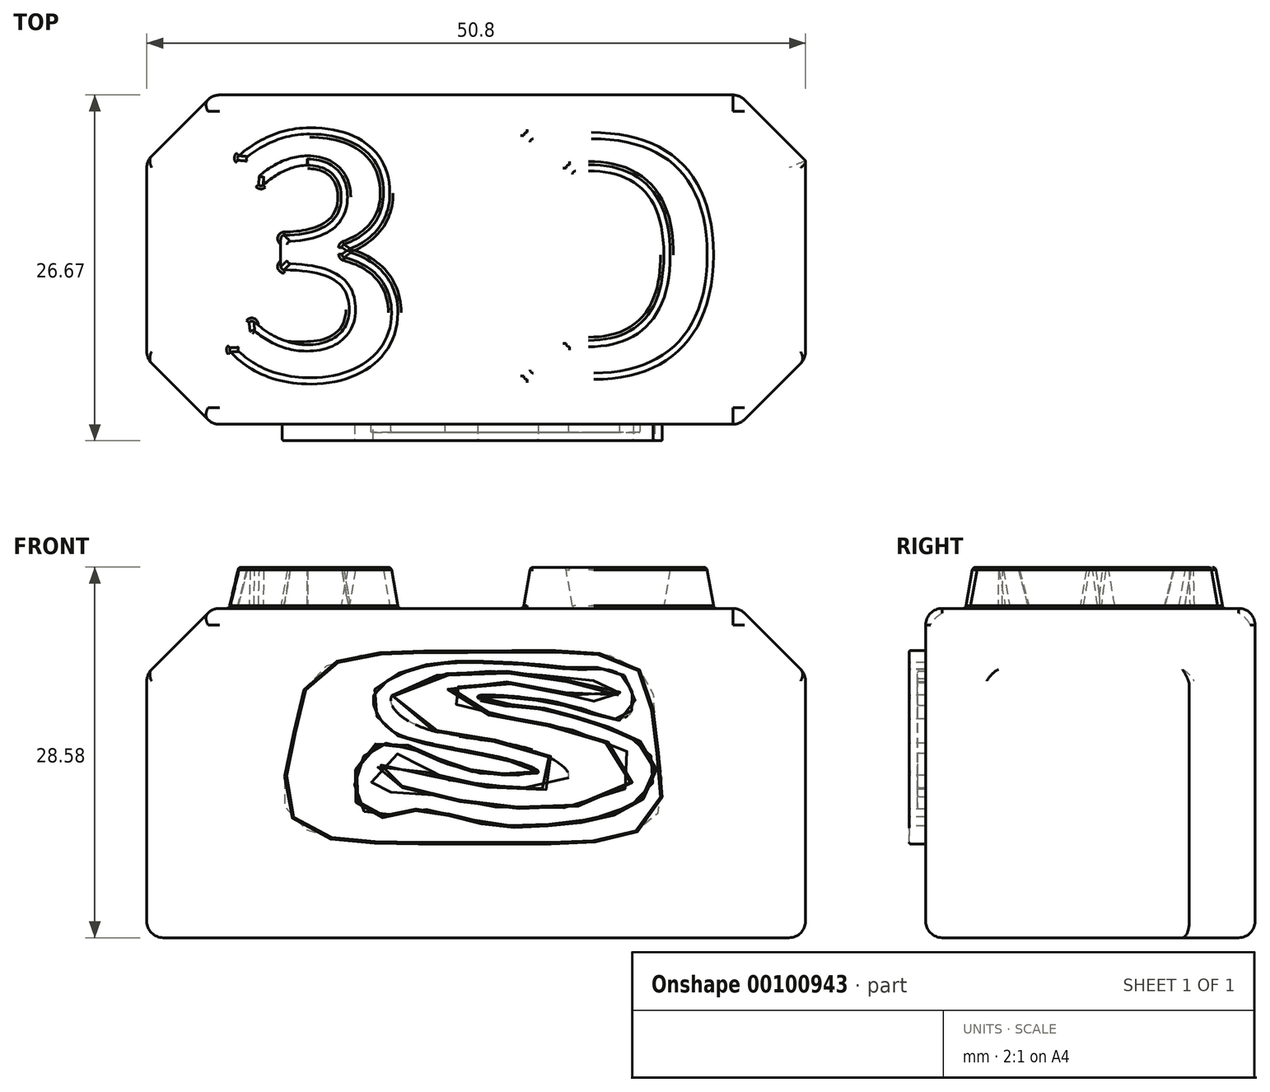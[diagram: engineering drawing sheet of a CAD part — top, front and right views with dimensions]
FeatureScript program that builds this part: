
annotation { "Feature Type Name" : "Feature", "Feature Type Description" : "" }
export const myFeature = defineFeature(function(context is Context, id is Id, definition is map)
    precondition{}
    {
        {
            var Q0;
            Q0=qCreatedBy(makeId("Top.planeOp"),FACE);
            var sketch = newSketch(context, id + "F0", { "sketchPlane" : qUnion([Q0])});
            skLineSegment(sketch, "E0.bottom", {"start": v(0, 0) * mm, "end": v(50.8, 0) * mm});
            skLineSegment(sketch, "E0.top", {"start": v(0, -25.4) * mm, "end": v(50.8, -25.4) * mm});
            skLineSegment(sketch, "E0.left", {"start": v(0, 0) * mm, "end": v(0, -25.4) * mm});
            skLineSegment(sketch, "E0.right", {"start": v(50.8, 0) * mm, "end": v(50.8, -25.4) * mm});
            skSolve(sketch);
        }
        {
            var Q0;
            Q0=makeQuery(id+"F0.imprint","IMPRINT",FACE,{"disambiguationData":[TD([[makeQuery(id+"F0.imprint","IMPRINT",EDGE,{"derivedFrom":sQuery(id+"F0.wireOp",EDGE,"E0.bottom")}),-1.0]])]});
            extrude(context, id + "F1", {"entities" : qUnion([Q0]), "depth" : 25.4 * mm});
        }
        {
            var Q0;
            Q0=makeQuery(id+"F1.opExtrude","CAP_EDGE",EDGE,{"disambiguationData":[OSD([sQuery(id+"F0.wireOp",EDGE,"E0.left")])],"isStart":false});
            var Q1;
            Q1=makeQuery(id+"F1.opExtrude","CAP_EDGE",EDGE,{"disambiguationData":[OSD([sQuery(id+"F0.wireOp",EDGE,"E0.right")])],"isStart":false});
            var Q2;
            Q2=makeQuery(id+"F1.opExtrude","SWEPT_EDGE",EDGE,{"disambiguationData":[OSD([sQuery(id+"F0.wireOp",EDGE,"E0.top"),sQuery(id+"F0.wireOp",EDGE,"E0.left")])]});
            var Q3;
            Q3=makeQuery(id+"F1.opExtrude","SWEPT_EDGE",EDGE,{"disambiguationData":[OSD([sQuery(id+"F0.wireOp",EDGE,"E0.top"),sQuery(id+"F0.wireOp",EDGE,"E0.right")])]});
            var Q4;
            Q4=makeQuery(id+"F1.opExtrude","SWEPT_EDGE",EDGE,{"disambiguationData":[OSD([sQuery(id+"F0.wireOp",EDGE,"E0.bottom"),sQuery(id+"F0.wireOp",EDGE,"E0.right")])]});
            var Q5;
            Q5=makeQuery(id+"F1.opExtrude","SWEPT_EDGE",EDGE,{"disambiguationData":[OSD([sQuery(id+"F0.wireOp",EDGE,"E0.bottom"),sQuery(id+"F0.wireOp",EDGE,"E0.left")])]});
            chamfer(context, id + "F2", {"entities" : qUnion([Q0, Q1, Q2, Q3, Q4, Q5]), "width" : 5.08 * mm, "tangentPropagation" : true});
        }
        {
            var Q0;
            Q0=makeQuery(id+"F1.opExtrude","CAP_EDGE",EDGE,{"disambiguationData":[OSD([sQuery(id+"F0.wireOp",EDGE,"E0.top")])],"isStart":false});
            var Q1;
            Q1=makeQuery(id+"F1.opExtrude","CAP_EDGE",EDGE,{"disambiguationData":[OSD([sQuery(id+"F0.wireOp",EDGE,"E0.bottom")])],"isStart":false});
            var Q2;
            {var subQ0=sQuery(id+"F0.wireOp",EDGE,"E0.right");var subQ1=sQuery(id+"F0.wireOp",EDGE,"E0.left");var subQ2=sQuery(id+"F0.wireOp",EDGE,"E0.top");var subQ3=sQuery(id+"F0.wireOp",EDGE,"E0.bottom");Q2=makeQuery(id+"F2.opChamfer","BLEND_EDGE",EDGE,{"blendedFrom":[makeQuery(id+"F1.opExtrude","CAP_EDGE",EDGE,{"disambiguationData":[OSD([subQ0])],"isStart":false}),makeQuery(id+"FMAaeaN72eKezCo_1.boolean.opBoolean","SPLIT",FACE,{"disambiguationData":[TD([makeQuery(id+"F1.opExtrude","SWEPT_FACE",FACE,{"disambiguationData":[OSD([subQ3])]})])],"derivedFrom":makeQuery(id+"F1.opExtrude","CAP_FACE",FACE,{"disambiguationData":[OSD([subQ3,subQ2,subQ1,subQ0])],"isStart":false})})],"blendedInto":[makeQuery(id+"FMAaeaN72eKezCo_1.boolean.opBoolean","SPLIT",FACE,{"disambiguationData":[TD([makeQuery(id+"F1.opExtrude","SWEPT_FACE",FACE,{"disambiguationData":[OSD([subQ3])]})])],"derivedFrom":makeQuery(id+"F1.opExtrude","CAP_FACE",FACE,{"disambiguationData":[OSD([subQ3,subQ2,subQ1,subQ0])],"isStart":false})})]});}
            var Q3;
            {var subQ0=sQuery(id+"F0.wireOp",EDGE,"E0.right");Q3=makeQuery(id+"F2.opChamfer","BLEND_EDGE",EDGE,{"blendedFrom":[makeQuery(id+"F1.opExtrude","SWEPT_EDGE",EDGE,{"disambiguationData":[OSD([sQuery(id+"F0.wireOp",EDGE,"E0.bottom"),subQ0])]}),makeQuery(id+"F1.opExtrude","CAP_EDGE",EDGE,{"disambiguationData":[OSD([subQ0])],"isStart":false})],"blendedInto":[]});}
            var Q4;
            {var subQ0=sQuery(id+"F0.wireOp",EDGE,"E0.right");Q4=makeQuery(id+"F2.opChamfer","BLEND_EDGE",EDGE,{"blendedFrom":[makeQuery(id+"F1.opExtrude","SWEPT_EDGE",EDGE,{"disambiguationData":[OSD([sQuery(id+"F0.wireOp",EDGE,"E0.top"),subQ0])]}),makeQuery(id+"F1.opExtrude","CAP_EDGE",EDGE,{"disambiguationData":[OSD([subQ0])],"isStart":false})],"blendedInto":[]});}
            var Q5;
            {var subQ0=sQuery(id+"F0.wireOp",EDGE,"E0.top");Q5=makeQuery(id+"F2.opChamfer","BLEND_EDGE",EDGE,{"blendedFrom":[makeQuery(id+"F1.opExtrude","SWEPT_EDGE",EDGE,{"disambiguationData":[OSD([subQ0,sQuery(id+"F0.wireOp",EDGE,"E0.right")])]}),makeQuery(id+"F1.opExtrude","SWEPT_FACE",FACE,{"disambiguationData":[OSD([subQ0])]})],"blendedInto":[makeQuery(id+"F1.opExtrude","SWEPT_FACE",FACE,{"disambiguationData":[OSD([subQ0])]})]});}
            var Q6;
            Q6=makeQuery(id+"F1.opExtrude","CAP_EDGE",EDGE,{"disambiguationData":[OSD([sQuery(id+"F0.wireOp",EDGE,"E0.right")])],"isStart":true});
            var Q7;
            {var subQ0=sQuery(id+"F0.wireOp",EDGE,"E0.top");Q7=makeQuery(id+"F2.opChamfer","BLEND_EDGE",EDGE,{"blendedFrom":[makeQuery(id+"F1.opExtrude","SWEPT_EDGE",EDGE,{"disambiguationData":[OSD([subQ0,sQuery(id+"F0.wireOp",EDGE,"E0.left")])]}),makeQuery(id+"F1.opExtrude","SWEPT_FACE",FACE,{"disambiguationData":[OSD([subQ0])]})],"blendedInto":[makeQuery(id+"F1.opExtrude","SWEPT_FACE",FACE,{"disambiguationData":[OSD([subQ0])]})]});}
            var Q8;
            {var subQ0=sQuery(id+"F0.wireOp",EDGE,"E0.left");Q8=makeQuery(id+"F2.opChamfer","BLEND_EDGE",EDGE,{"blendedFrom":[makeQuery(id+"F1.opExtrude","SWEPT_EDGE",EDGE,{"disambiguationData":[OSD([sQuery(id+"F0.wireOp",EDGE,"E0.top"),subQ0])]}),makeQuery(id+"F1.opExtrude","SWEPT_FACE",FACE,{"disambiguationData":[OSD([subQ0])]})],"blendedInto":[makeQuery(id+"F1.opExtrude","SWEPT_FACE",FACE,{"disambiguationData":[OSD([subQ0])]})]});}
            var Q9;
            {var subQ0=sQuery(id+"F0.wireOp",EDGE,"E0.left");Q9=makeQuery(id+"F2.opChamfer","BLEND_EDGE",EDGE,{"blendedFrom":[makeQuery(id+"F1.opExtrude","SWEPT_EDGE",EDGE,{"disambiguationData":[OSD([sQuery(id+"F0.wireOp",EDGE,"E0.top"),subQ0])]}),makeQuery(id+"F1.opExtrude","CAP_EDGE",EDGE,{"disambiguationData":[OSD([subQ0])],"isStart":false})],"blendedInto":[]});}
            var Q10;
            {var subQ0=sQuery(id+"F0.wireOp",EDGE,"E0.right");var subQ1=sQuery(id+"F0.wireOp",EDGE,"E0.left");var subQ2=sQuery(id+"F0.wireOp",EDGE,"E0.top");var subQ3=sQuery(id+"F0.wireOp",EDGE,"E0.bottom");Q10=makeQuery(id+"F2.opChamfer","BLEND_EDGE",EDGE,{"blendedFrom":[makeQuery(id+"F1.opExtrude","CAP_EDGE",EDGE,{"disambiguationData":[OSD([subQ1])],"isStart":false}),makeQuery(id+"FMAaeaN72eKezCo_1.boolean.opBoolean","SPLIT",FACE,{"disambiguationData":[TD([makeQuery(id+"F1.opExtrude","SWEPT_FACE",FACE,{"disambiguationData":[OSD([subQ3])]})])],"derivedFrom":makeQuery(id+"F1.opExtrude","CAP_FACE",FACE,{"disambiguationData":[OSD([subQ3,subQ2,subQ1,subQ0])],"isStart":false})})],"blendedInto":[makeQuery(id+"FMAaeaN72eKezCo_1.boolean.opBoolean","SPLIT",FACE,{"disambiguationData":[TD([makeQuery(id+"F1.opExtrude","SWEPT_FACE",FACE,{"disambiguationData":[OSD([subQ3])]})])],"derivedFrom":makeQuery(id+"F1.opExtrude","CAP_FACE",FACE,{"disambiguationData":[OSD([subQ3,subQ2,subQ1,subQ0])],"isStart":false})})]});}
            var Q11;
            {var subQ0=sQuery(id+"F0.wireOp",EDGE,"E0.left");Q11=makeQuery(id+"F2.opChamfer","BLEND_EDGE",EDGE,{"blendedFrom":[makeQuery(id+"F1.opExtrude","CAP_EDGE",EDGE,{"disambiguationData":[OSD([subQ0])],"isStart":false}),makeQuery(id+"F1.opExtrude","SWEPT_FACE",FACE,{"disambiguationData":[OSD([subQ0])]})],"blendedInto":[makeQuery(id+"F1.opExtrude","SWEPT_FACE",FACE,{"disambiguationData":[OSD([subQ0])]})]});}
            var Q12;
            {var subQ0=sQuery(id+"F0.wireOp",EDGE,"E0.left");Q12=makeQuery(id+"F2.opChamfer","BLEND_EDGE",EDGE,{"blendedFrom":[makeQuery(id+"F1.opExtrude","SWEPT_EDGE",EDGE,{"disambiguationData":[OSD([sQuery(id+"F0.wireOp",EDGE,"E0.bottom"),subQ0])]}),makeQuery(id+"F1.opExtrude","CAP_EDGE",EDGE,{"disambiguationData":[OSD([subQ0])],"isStart":false})],"blendedInto":[]});}
            var Q13;
            {var subQ0=sQuery(id+"F0.wireOp",EDGE,"E0.left");Q13=makeQuery(id+"F2.opChamfer","BLEND_EDGE",EDGE,{"blendedFrom":[makeQuery(id+"F1.opExtrude","SWEPT_EDGE",EDGE,{"disambiguationData":[OSD([sQuery(id+"F0.wireOp",EDGE,"E0.bottom"),subQ0])]}),makeQuery(id+"F1.opExtrude","SWEPT_FACE",FACE,{"disambiguationData":[OSD([subQ0])]})],"blendedInto":[makeQuery(id+"F1.opExtrude","SWEPT_FACE",FACE,{"disambiguationData":[OSD([subQ0])]})]});}
            var Q14;
            {var subQ0=sQuery(id+"F0.wireOp",EDGE,"E0.bottom");Q14=makeQuery(id+"F2.opChamfer","BLEND_EDGE",EDGE,{"blendedFrom":[makeQuery(id+"F1.opExtrude","SWEPT_EDGE",EDGE,{"disambiguationData":[OSD([subQ0,sQuery(id+"F0.wireOp",EDGE,"E0.left")])]}),makeQuery(id+"F1.opExtrude","SWEPT_FACE",FACE,{"disambiguationData":[OSD([subQ0])]})],"blendedInto":[makeQuery(id+"F1.opExtrude","SWEPT_FACE",FACE,{"disambiguationData":[OSD([subQ0])]})]});}
            var Q15;
            {var subQ0=sQuery(id+"F0.wireOp",EDGE,"E0.bottom");Q15=makeQuery(id+"F2.opChamfer","BLEND_EDGE",EDGE,{"blendedFrom":[makeQuery(id+"F1.opExtrude","SWEPT_EDGE",EDGE,{"disambiguationData":[OSD([subQ0,sQuery(id+"F0.wireOp",EDGE,"E0.right")])]}),makeQuery(id+"F1.opExtrude","SWEPT_FACE",FACE,{"disambiguationData":[OSD([subQ0])]})],"blendedInto":[makeQuery(id+"F1.opExtrude","SWEPT_FACE",FACE,{"disambiguationData":[OSD([subQ0])]})]});}
            var Q16;
            {var subQ0=sQuery(id+"F0.wireOp",EDGE,"E0.right");Q16=makeQuery(id+"F2.opChamfer","BLEND_EDGE",EDGE,{"blendedFrom":[makeQuery(id+"F1.opExtrude","SWEPT_EDGE",EDGE,{"disambiguationData":[OSD([sQuery(id+"F0.wireOp",EDGE,"E0.top"),subQ0])]}),makeQuery(id+"F1.opExtrude","SWEPT_FACE",FACE,{"disambiguationData":[OSD([subQ0])]})],"blendedInto":[makeQuery(id+"F1.opExtrude","SWEPT_FACE",FACE,{"disambiguationData":[OSD([subQ0])]})]});}
            var Q17;
            {var subQ0=sQuery(id+"F0.wireOp",EDGE,"E0.right");Q17=makeQuery(id+"F2.opChamfer","BLEND_EDGE",EDGE,{"blendedFrom":[makeQuery(id+"F1.opExtrude","CAP_EDGE",EDGE,{"disambiguationData":[OSD([subQ0])],"isStart":false}),makeQuery(id+"F1.opExtrude","SWEPT_FACE",FACE,{"disambiguationData":[OSD([subQ0])]})],"blendedInto":[makeQuery(id+"F1.opExtrude","SWEPT_FACE",FACE,{"disambiguationData":[OSD([subQ0])]})]});}
            var Q18;
            {var subQ0=sQuery(id+"F0.wireOp",EDGE,"E0.left");var subQ1=sQuery(id+"F0.wireOp",EDGE,"E0.bottom");Q18=makeQuery(id+"F2.opChamfer","BLEND_EDGE",EDGE,{"blendedFrom":[makeQuery(id+"F1.opExtrude","SWEPT_EDGE",EDGE,{"disambiguationData":[OSD([subQ1,subQ0])]}),makeQuery(id+"F1.opExtrude","CAP_FACE",FACE,{"disambiguationData":[OSD([subQ1,sQuery(id+"F0.wireOp",EDGE,"E0.top"),subQ0,sQuery(id+"F0.wireOp",EDGE,"E0.right")])],"isStart":true})],"blendedInto":[makeQuery(id+"F1.opExtrude","CAP_FACE",FACE,{"disambiguationData":[OSD([subQ1,sQuery(id+"F0.wireOp",EDGE,"E0.top"),subQ0,sQuery(id+"F0.wireOp",EDGE,"E0.right")])],"isStart":true})]});}
            var Q19;
            Q19=makeQuery(id+"F1.opExtrude","CAP_EDGE",EDGE,{"disambiguationData":[OSD([sQuery(id+"F0.wireOp",EDGE,"E0.left")])],"isStart":true});
            var Q20;
            Q20=makeQuery(id+"F1.opExtrude","CAP_EDGE",EDGE,{"disambiguationData":[OSD([sQuery(id+"F0.wireOp",EDGE,"E0.bottom")])],"isStart":true});
            var Q21;
            {var subQ0=sQuery(id+"F0.wireOp",EDGE,"E0.right");var subQ1=sQuery(id+"F0.wireOp",EDGE,"E0.bottom");Q21=makeQuery(id+"F2.opChamfer","BLEND_EDGE",EDGE,{"blendedFrom":[makeQuery(id+"F1.opExtrude","SWEPT_EDGE",EDGE,{"disambiguationData":[OSD([subQ1,subQ0])]}),makeQuery(id+"F1.opExtrude","CAP_FACE",FACE,{"disambiguationData":[OSD([subQ1,sQuery(id+"F0.wireOp",EDGE,"E0.top"),sQuery(id+"F0.wireOp",EDGE,"E0.left"),subQ0])],"isStart":true})],"blendedInto":[makeQuery(id+"F1.opExtrude","CAP_FACE",FACE,{"disambiguationData":[OSD([subQ1,sQuery(id+"F0.wireOp",EDGE,"E0.top"),sQuery(id+"F0.wireOp",EDGE,"E0.left"),subQ0])],"isStart":true})]});}
            var Q22;
            {var subQ0=sQuery(id+"F0.wireOp",EDGE,"E0.right");var subQ1=sQuery(id+"F0.wireOp",EDGE,"E0.top");Q22=makeQuery(id+"F2.opChamfer","BLEND_EDGE",EDGE,{"blendedFrom":[makeQuery(id+"F1.opExtrude","SWEPT_EDGE",EDGE,{"disambiguationData":[OSD([subQ1,subQ0])]}),makeQuery(id+"F1.opExtrude","CAP_FACE",FACE,{"disambiguationData":[OSD([sQuery(id+"F0.wireOp",EDGE,"E0.bottom"),subQ1,sQuery(id+"F0.wireOp",EDGE,"E0.left"),subQ0])],"isStart":true})],"blendedInto":[makeQuery(id+"F1.opExtrude","CAP_FACE",FACE,{"disambiguationData":[OSD([sQuery(id+"F0.wireOp",EDGE,"E0.bottom"),subQ1,sQuery(id+"F0.wireOp",EDGE,"E0.left"),subQ0])],"isStart":true})]});}
            var Q23;
            Q23=makeQuery(id+"F1.opExtrude","CAP_EDGE",EDGE,{"disambiguationData":[OSD([sQuery(id+"F0.wireOp",EDGE,"E0.top")])],"isStart":true});
            var Q24;
            {var subQ0=sQuery(id+"F0.wireOp",EDGE,"E0.left");var subQ1=sQuery(id+"F0.wireOp",EDGE,"E0.top");Q24=makeQuery(id+"F2.opChamfer","BLEND_EDGE",EDGE,{"blendedFrom":[makeQuery(id+"F1.opExtrude","SWEPT_EDGE",EDGE,{"disambiguationData":[OSD([subQ1,subQ0])]}),makeQuery(id+"F1.opExtrude","CAP_FACE",FACE,{"disambiguationData":[OSD([sQuery(id+"F0.wireOp",EDGE,"E0.bottom"),subQ1,subQ0,sQuery(id+"F0.wireOp",EDGE,"E0.right")])],"isStart":true})],"blendedInto":[makeQuery(id+"F1.opExtrude","CAP_FACE",FACE,{"disambiguationData":[OSD([sQuery(id+"F0.wireOp",EDGE,"E0.bottom"),subQ1,subQ0,sQuery(id+"F0.wireOp",EDGE,"E0.right")])],"isStart":true})]});}
            fillet(context, id + "F3", {"entities" : qUnion([Q0, Q1, Q2, Q3, Q4, Q5, Q6, Q7, Q8, Q9, Q10, Q11, Q12, Q13, Q14, Q15, Q16, Q17, Q18, Q19, Q20, Q21, Q22, Q23, Q24]), "radius" : 1.27 * mm, "tangentPropagation" : true, "allowEdgeOverflow" : false});
        }
        {
            var Q0;
            Q0=makeQuery(id+"F1.opExtrude","CAP_FACE",FACE,{"disambiguationData":[OSD([sQuery(id+"F0.wireOp",EDGE,"E0.bottom"),sQuery(id+"F0.wireOp",EDGE,"E0.top"),sQuery(id+"F0.wireOp",EDGE,"E0.left"),sQuery(id+"F0.wireOp",EDGE,"E0.right")])],"isStart":false});
            var sketch = newSketch(context, id + "F4", { "sketchPlane" : qUnion([Q0])});
            skText(sketch, "E1", { "text": "3 D", "fontName": "NotoSansCJKsc-Bold.otf"});
            const initialGuessF4  = {"E1": [0.0056, -0.02197, 1, 0, 0.0186]};
            skSetInitialGuess(sketch, initialGuessF4);
            skSolve(sketch);
        }
        {
            var Q0;
            Q0 = qSketchRegion(id + "F4", true);
            extrude(context, id + "F5", {"entities" : qUnion([Q0]), "operationType" : NewBodyOperationType.ADD, "depth" : 3.17 * mm, "hasDraft" : true, "draftAngle" : 10 * degree, "draftPullDirection" : true});
        }
        {
            var Q0;
            Q0=makeQuery(id+"F5.opExtrude","CAP_FACE",FACE,{"disambiguationData":[OSD([sQuery(id+"F4.wireOp",EDGE,"E1.sketch_text.stroke-0"),sQuery(id+"F4.wireOp",EDGE,"E1.sketch_text.stroke-1"),sQuery(id+"F4.wireOp",EDGE,"E1.sketch_text.stroke-2"),sQuery(id+"F4.wireOp",EDGE,"E1.sketch_text.stroke-3"),sQuery(id+"F4.wireOp",EDGE,"E1.sketch_text.stroke-4"),sQuery(id+"F4.wireOp",EDGE,"E1.sketch_text.stroke-5"),sQuery(id+"F4.wireOp",EDGE,"E1.sketch_text.stroke-6"),sQuery(id+"F4.wireOp",EDGE,"E1.sketch_text.stroke-7"),sQuery(id+"F4.wireOp",EDGE,"E1.sketch_text.stroke-8"),sQuery(id+"F4.wireOp",EDGE,"E1.sketch_text.stroke-9"),sQuery(id+"F4.wireOp",EDGE,"E1.sketch_text.stroke-10"),sQuery(id+"F4.wireOp",EDGE,"E1.sketch_text.stroke-11"),sQuery(id+"F4.wireOp",EDGE,"E1.sketch_text.stroke-12"),sQuery(id+"F4.wireOp",EDGE,"E1.sketch_text.stroke-13"),sQuery(id+"F4.wireOp",EDGE,"E1.sketch_text.stroke-14"),sQuery(id+"F4.wireOp",EDGE,"E1.sketch_text.stroke-15")])],"isStart":false});
            var Q1;
            Q1=makeQuery(id+"F5.opExtrude","SWEPT_FACE",FACE,{"disambiguationData":[OSD([sQuery(id+"F4.wireOp",EDGE,"E1.sketch_text.stroke-6")])]});
            var Q2;
            Q2=makeQuery(id+"F5.opExtrude","CAP_EDGE",EDGE,{"disambiguationData":[OSD([sQuery(id+"F4.wireOp",EDGE,"E1.sketch_text.stroke-11")])],"isStart":true});
            var Q3;
            Q3=makeQuery(id+"F5.opExtrude","SWEPT_FACE",FACE,{"disambiguationData":[OSD([sQuery(id+"F4.wireOp",EDGE,"E1.sketch_text.stroke-11")])]});
            var Q4;
            Q4=makeQuery(id+"F5.opExtrude","SWEPT_FACE",FACE,{"disambiguationData":[OSD([sQuery(id+"F4.wireOp",EDGE,"E1.sketch_text.stroke-7")])]});
            var Q5;
            Q5=makeQuery(id+"F5.opExtrude","SWEPT_FACE",FACE,{"disambiguationData":[OSD([sQuery(id+"F4.wireOp",EDGE,"E1.sketch_text.stroke-8")])]});
            var Q6;
            Q6=makeQuery(id+"F5.opExtrude","SWEPT_FACE",FACE,{"disambiguationData":[OSD([sQuery(id+"F4.wireOp",EDGE,"E1.sketch_text.stroke-9")])]});
            var Q7;
            Q7=makeQuery(id+"F5.opExtrude","SWEPT_FACE",FACE,{"disambiguationData":[OSD([sQuery(id+"F4.wireOp",EDGE,"E1.sketch_text.stroke-12")])]});
            var Q8;
            Q8=makeQuery(id+"F5.opExtrude","SWEPT_FACE",FACE,{"disambiguationData":[OSD([sQuery(id+"F4.wireOp",EDGE,"E1.sketch_text.stroke-14")])]});
            var Q9;
            Q9=makeQuery(id+"F5.opExtrude","SWEPT_FACE",FACE,{"disambiguationData":[OSD([sQuery(id+"F4.wireOp",EDGE,"E1.sketch_text.stroke-5")])]});
            var Q10;
            Q10=makeQuery(id+"F5.opExtrude","SWEPT_FACE",FACE,{"disambiguationData":[OSD([sQuery(id+"F4.wireOp",EDGE,"E1.sketch_text.stroke-4")])]});
            var Q11;
            Q11=makeQuery(id+"F5.opExtrude","SWEPT_FACE",FACE,{"disambiguationData":[OSD([sQuery(id+"F4.wireOp",EDGE,"E1.sketch_text.stroke-3")])]});
            var Q12;
            Q12=makeQuery(id+"F5.opExtrude","SWEPT_FACE",FACE,{"disambiguationData":[OSD([sQuery(id+"F4.wireOp",EDGE,"E1.sketch_text.stroke-1")])]});
            var Q13;
            Q13=makeQuery(id+"F5.opExtrude","SWEPT_FACE",FACE,{"disambiguationData":[OSD([sQuery(id+"F4.wireOp",EDGE,"E1.sketch_text.stroke-0")])]});
            var Q14;
            Q14=makeQuery(id+"F5.opExtrude","SWEPT_FACE",FACE,{"disambiguationData":[OSD([sQuery(id+"F4.wireOp",EDGE,"E1.sketch_text.stroke-15")])]});
            var Q15;
            Q15=makeQuery(id+"F5.opExtrude","CAP_EDGE",EDGE,{"disambiguationData":[OSD([sQuery(id+"F4.wireOp",EDGE,"E1.sketch_text.stroke-13")])],"isStart":true});
            var Q16;
            Q16=makeQuery(id+"F5.opExtrude","CAP_EDGE",EDGE,{"disambiguationData":[OSD([sQuery(id+"F4.wireOp",EDGE,"E1.sketch_text.stroke-10")])],"isStart":true});
            fillet(context, id + "F6", {"entities" : qUnion([Q0, Q1, Q2, Q3, Q4, Q5, Q6, Q7, Q8, Q9, Q10, Q11, Q12, Q13, Q14, Q15, Q16]), "radius" : 0.25 * mm, "allowEdgeOverflow" : false});
        }
        {
            var Q0;
            Q0=makeQuery(id+"F5.opExtrude","CAP_FACE",FACE,{"disambiguationData":[OSD([sQuery(id+"F4.wireOp",EDGE,"E1.sketch_text.stroke-16"),sQuery(id+"F4.wireOp",EDGE,"E1.sketch_text.stroke-17"),sQuery(id+"F4.wireOp",EDGE,"E1.sketch_text.stroke-18"),sQuery(id+"F4.wireOp",EDGE,"E1.sketch_text.stroke-19"),sQuery(id+"F4.wireOp",EDGE,"E1.sketch_text.stroke-20"),sQuery(id+"F4.wireOp",EDGE,"E1.sketch_text.stroke-21"),sQuery(id+"F4.wireOp",EDGE,"E1.sketch_text.stroke-22"),sQuery(id+"F4.wireOp",EDGE,"E1.sketch_text.stroke-23"),sQuery(id+"F4.wireOp",EDGE,"E1.sketch_text.stroke-24"),sQuery(id+"F4.wireOp",EDGE,"E1.sketch_text.stroke-25")])],"isStart":false});
            var Q1;
            Q1=makeQuery(id+"F5.opExtrude","CAP_EDGE",EDGE,{"disambiguationData":[OSD([sQuery(id+"F4.wireOp",EDGE,"E1.sketch_text.stroke-19")])],"isStart":true});
            var Q2;
            Q2=makeQuery(id+"F5.opExtrude","SWEPT_FACE",FACE,{"disambiguationData":[OSD([sQuery(id+"F4.wireOp",EDGE,"E1.sketch_text.stroke-18")])]});
            var Q3;
            Q3=makeQuery(id+"F5.opExtrude","CAP_EDGE",EDGE,{"disambiguationData":[OSD([sQuery(id+"F4.wireOp",EDGE,"E1.sketch_text.stroke-17")])],"isStart":true});
            var Q4;
            Q4=makeQuery(id+"F5.opExtrude","SWEPT_FACE",FACE,{"disambiguationData":[OSD([sQuery(id+"F4.wireOp",EDGE,"E1.sketch_text.stroke-16")])]});
            var Q5;
            Q5=makeQuery(id+"F5.opExtrude","SWEPT_FACE",FACE,{"disambiguationData":[OSD([sQuery(id+"F4.wireOp",EDGE,"E1.sketch_text.stroke-20")])]});
            var Q6;
            Q6=makeQuery(id+"F5.opExtrude","SWEPT_FACE",FACE,{"disambiguationData":[OSD([sQuery(id+"F4.wireOp",EDGE,"E1.sketch_text.stroke-21")])]});
            var Q7;
            Q7=makeQuery(id+"F5.opExtrude","SWEPT_FACE",FACE,{"disambiguationData":[OSD([sQuery(id+"F4.wireOp",EDGE,"E1.sketch_text.stroke-22")])]});
            var Q8;
            Q8=makeQuery(id+"F5.opExtrude","SWEPT_FACE",FACE,{"disambiguationData":[OSD([sQuery(id+"F4.wireOp",EDGE,"E1.sketch_text.stroke-23")])]});
            fillet(context, id + "F7", {"entities" : qUnion([Q0, Q1, Q2, Q3, Q4, Q5, Q6, Q7, Q8]), "radius" : 0.25 * mm, "tangentPropagation" : true, "allowEdgeOverflow" : false});
        }
        {
            var Q0;
            Q0=makeQuery(id+"F1.opExtrude","SWEPT_FACE",FACE,{"disambiguationData":[OSD([sQuery(id+"F0.wireOp",EDGE,"E0.top")])]});
            var sketch = newSketch(context, id + "F8", { "sketchPlane" : qUnion([Q0])});
            skFitSpline(sketch, "E2", {"points": [v(12.12, 19.14) * mm, v(14.19, 21.12) * mm, v(18.19, 22) * mm, v(25.87, 22.13) * mm, v(33.54, 22.09) * mm, v(36.76, 21.4) * mm, v(38.83, 19.74) * mm, v(39.06, 17.26) * mm, v(39.75, 11.74) * mm, v(38.97, 8.98) * mm, v(35.57, 7.51) * mm, v(26.7, 7.23) * mm, v(15.47, 7.42) * mm, v(12.07, 8.48) * mm, v(10.5, 10.55) * mm, v(11.01, 14.04) * mm, v(12.12, 19.14) * mm]});
            skFitSpline(sketch, "E3", {"points": [v(17.5, 18.68) * mm, v(19.61, 20.34) * mm, v(23.18, 21.17) * mm, v(26.93, 21.17) * mm, v(30.06, 20.97) * mm, v(33.15, 20.68) * mm, v(35.24, 20.7) * mm, v(37.03, 19.83) * mm, v(37.42, 17.57) * mm, v(36.38, 16.88) * mm, v(33.9, 17.55) * mm, v(30.31, 18.4) * mm, v(26.45, 18.72) * mm, v(25.52, 18.6) * mm, v(25.9, 18.17) * mm, v(28.15, 17.85) * mm, v(30.81, 17.56) * mm, v(34.03, 16.65) * mm, v(37.4, 15.37) * mm, v(38.93, 13.94) * mm, v(38.9, 11.69) * mm, v(36.13, 9.62) * mm, v(30.56, 8.71) * mm, v(25.94, 8.89) * mm, v(20.46, 9.92) * mm, v(17.43, 9.37) * mm, v(16.1, 10.94) * mm, v(16.48, 13.6) * mm, v(18.14, 14.98) * mm, v(21.1, 14.32) * mm, v(24.07, 13.06) * mm, v(27.96, 12.53) * mm, v(30.2, 12.77) * mm, v(28.86, 13.48) * mm, v(24.76, 14.42) * mm, v(20.98, 15.2) * mm, v(18.86, 15.98) * mm, v(17.92, 17.03) * mm, v(17.5, 18.68) * mm]});
            skFitSpline(sketch, "E4", {"points": [v(18.9, 18.68) * mm, v(21.27, 20) * mm, v(24.35, 20.47) * mm, v(27.84, 20.55) * mm, v(30.88, 20.16) * mm, v(34.02, 19.77) * mm, v(35.56, 19.98) * mm, v(36.46, 19.14) * mm, v(36.07, 18.02) * mm, v(34.92, 18.1) * mm, v(32.66, 18.68) * mm, v(30.71, 19.14) * mm, v(28.08, 19.6) * mm, v(25.5, 19.62) * mm, v(23.42, 19.14) * mm, v(23.01, 18.68) * mm, v(24.13, 17.87) * mm, v(26.8, 17.22) * mm, v(31.97, 16.25) * mm, v(35.77, 15) * mm, v(38.04, 13.2) * mm, v(36, 10.96) * mm, v(31.2, 9.97) * mm, v(25.86, 10.19) * mm, v(21.71, 11.13) * mm, v(19.29, 11.51) * mm, v(18.23, 10.88) * mm, v(17.38, 11.36) * mm, v(17.5, 12.53) * mm, v(18.92, 14.24) * mm, v(21.28, 12.88) * mm, v(26.75, 11.7) * mm, v(31.46, 11.66) * mm, v(32.55, 12.53) * mm, v(30.7, 14.09) * mm, v(27.26, 15.06) * mm, v(22.14, 15.93) * mm, v(19.28, 17.4) * mm, v(18.9, 18.68) * mm]});
            skSolve(sketch);
        }
        {
            var Q0;
            Q0 = qSketchRegion(id + "F8", true);
            extrude(context, id + "F9", {"entities" : qUnion([Q0]), "operationType" : NewBodyOperationType.ADD, "depth" : 1.27 * mm});
        }
        {
            var Q0;
            Q0=makeQuery(id+"F9.opExtrude","CAP_EDGE",EDGE,{"disambiguationData":[OSD([sQuery(id+"F8.wireOp",EDGE,"E2")])],"isStart":false});
            var Q1;
            Q1=makeQuery(id+"F9.opExtrude","CAP_EDGE",EDGE,{"disambiguationData":[OSD([sQuery(id+"F8.wireOp",EDGE,"E3")])],"isStart":false});
            var Q2;
            Q2=makeQuery(id+"F9.opExtrude","CAP_EDGE",EDGE,{"disambiguationData":[OSD([sQuery(id+"F8.wireOp",EDGE,"E3")])],"isStart":true});
            var Q3;
            Q3=makeQuery(id+"F9.opExtrude","CAP_EDGE",EDGE,{"disambiguationData":[OSD([sQuery(id+"F8.wireOp",EDGE,"E2")])],"isStart":true});
            fillet(context, id + "F10", {"entities" : qUnion([Q0, Q1, Q2, Q3]), "radius" : 0.13 * mm, "tangentPropagation" : true, "allowEdgeOverflow" : false});
        }
        {
            var Q0;
            Q0=makeQuery(id+"F8.imprint","IMPRINT",FACE,{"disambiguationData":[TD([[makeQuery(id+"F8.imprint","IMPRINT",EDGE,{"derivedFrom":sQuery(id+"F8.wireOp",EDGE,"E4")}),-1.0]])]});
            extrude(context, id + "F11", {"entities" : qUnion([Q0]), "operationType" : NewBodyOperationType.ADD, "depth" : 0.64 * mm});
        }
        {
            var Q0;
            Q0=makeQuery(id+"F11.opExtrude","CAP_FACE",FACE,{"disambiguationData":[OSD([sQuery(id+"F8.wireOp",EDGE,"E4")])],"isStart":false});
            var Q1;
            Q1=makeQuery(id+"F11.opExtrude","CAP_EDGE",EDGE,{"disambiguationData":[OSD([sQuery(id+"F8.wireOp",EDGE,"E4")])],"isStart":true});
            fillet(context, id + "F12", {"entities" : qUnion([Q0, Q1]), "radius" : 0.13 * mm, "tangentPropagation" : true, "allowEdgeOverflow" : false});
        }
    });
